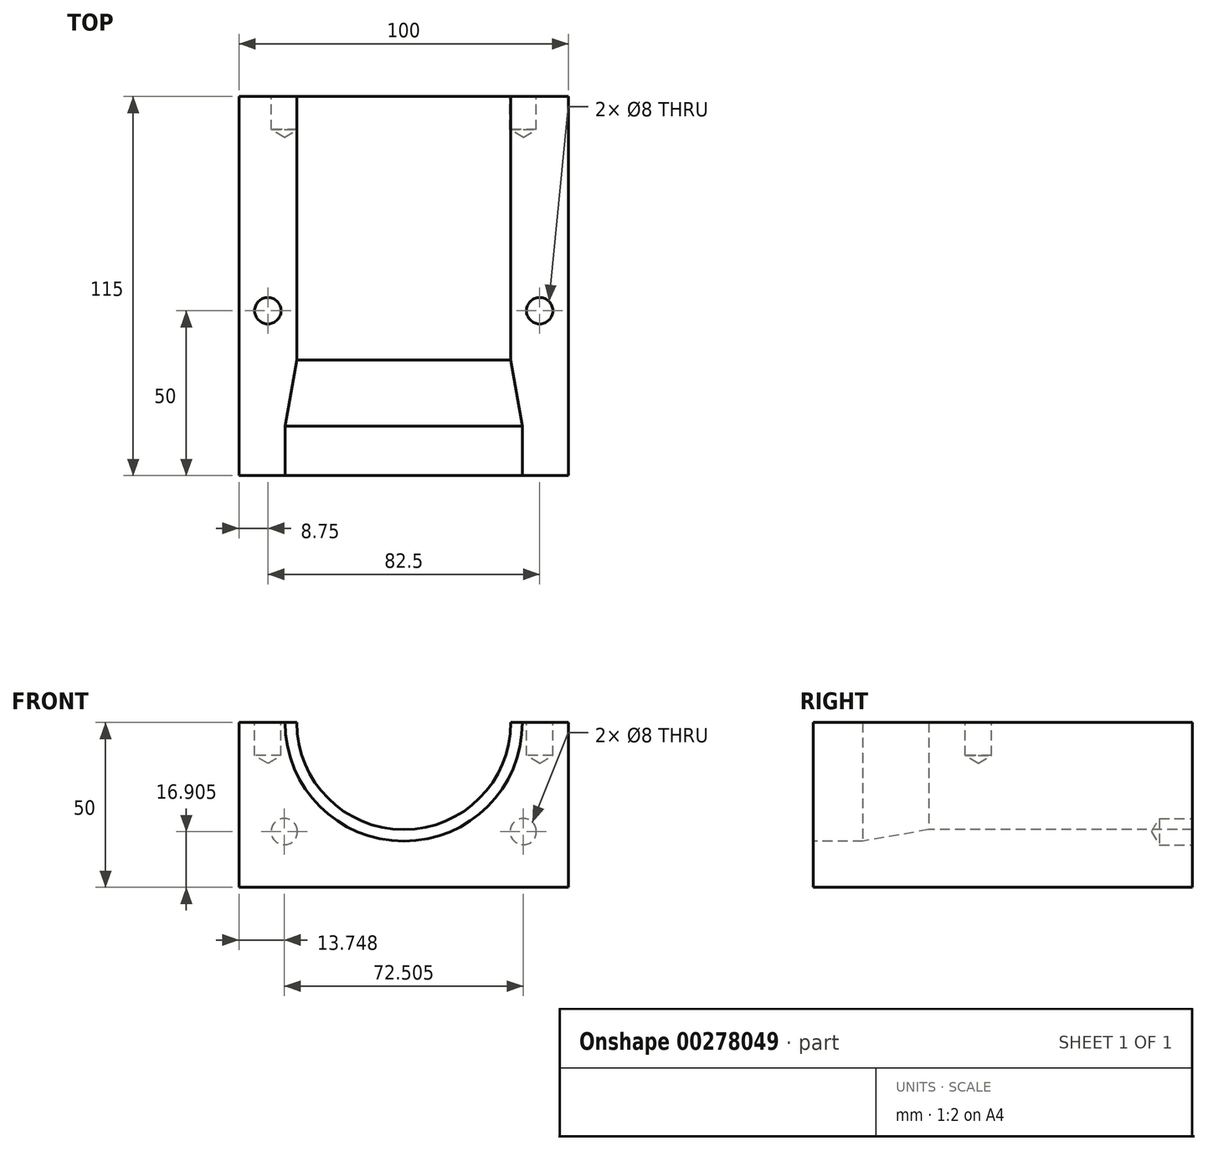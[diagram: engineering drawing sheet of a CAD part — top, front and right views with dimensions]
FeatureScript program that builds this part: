
annotation { "Feature Type Name" : "Feature", "Feature Type Description" : "" }
export const myFeature = defineFeature(function(context is Context, id is Id, definition is map)
    precondition{}
    {
        {
            var Q0;
            Q0=qCreatedBy(makeId("Top.planeOp"),FACE);
            var sketch = newSketch(context, id + "F0", { "sketchPlane" : qUnion([Q0])});
            skLineSegment(sketch, "E0", {"start": v(0, 0) * mm, "end": v(-36, 0) * mm});
            skLineSegment(sketch, "E1", {"start": v(-36, 0) * mm, "end": v(-36, 15) * mm});
            skLineSegment(sketch, "E2", {"start": v(-32.5, 35) * mm, "end": v(-32.5, 125) * mm});
            skLineSegment(sketch, "E3", {"start": v(-32.5, 125) * mm, "end": v(0, 125) * mm});
            skLineSegment(sketch, "E4", {"start": v(0, 125) * mm, "end": v(0, 0) * mm});
            skLineSegment(sketch, "E5", {"start": v(-36, 15) * mm, "end": v(-32.5, 35) * mm});
            skSolve(sketch);
        }
        {
            var Q0;
            Q0=qCreatedBy(makeId("Top.planeOp"),FACE);
            var sketch = newSketch(context, id + "F1", { "sketchPlane" : qUnion([Q0])});
            skLineSegment(sketch, "E6", {"start": v(0, 0) * mm, "end": v(50, 0) * mm});
            skLineSegment(sketch, "E7", {"start": v(50, 0) * mm, "end": v(50, 125) * mm});
            skLineSegment(sketch, "E8", {"start": v(50, 125) * mm, "end": v(-50, 125) * mm});
            skLineSegment(sketch, "E9", {"start": v(-50, 125) * mm, "end": v(-50, 0) * mm});
            skLineSegment(sketch, "E10", {"start": v(-50, 0) * mm, "end": v(0, 0) * mm});
            skSolve(sketch);
        }
        {
            var Q0;
            Q0 = qSketchRegion(id + "F1", true);
            extrude(context, id + "F2", {"entities" : qUnion([Q0]), "oppositeDirection" : true, "depth" : 50 * mm});
        }
        {
            var Q0;
            Q0 = qSketchRegion(id + "F0", true);
            var Q1;
            Q1=sQuery(id+"F0.wireOp",EDGE,"E4");
            revolve(context, id + "F3", {"operationType" : NewBodyOperationType.REMOVE, "entities" : qUnion([Q0]), "axis" : qUnion([Q1]), "revolveType" : RevolveType.FULL, "oppositeDirection" : true});
        }
        {
            var Q0;
            {var subQ0=sQuery(id+"F1.wireOp",EDGE,"E8");var subQ1=sQuery(id+"F1.wireOp",EDGE,"E7");var subQ2=sQuery(id+"F1.wireOp",EDGE,"E10");var subQ3=sQuery(id+"F1.wireOp",EDGE,"E6");Q0=makeQuery(id+"F3.boolean.opBoolean","SPLIT",FACE,{"disambiguationData":[TD([makeQuery(id+"F2.opExtrude","SWEPT_FACE",FACE,{"disambiguationData":[OSD([subQ1])]})])],"derivedFrom":makeQuery(id+"F2.opExtrude","CAP_FACE",FACE,{"disambiguationData":[OSD([subQ3,subQ1,subQ0,sQuery(id+"F1.wireOp",EDGE,"E9"),subQ2])],"isStart":true})});}
            var sketch = newSketch(context, id + "F4", { "sketchPlane" : qUnion([Q0])});
            skLineSegment(sketch, "E11", {"start": v(-41.25, 125) * mm, "end": v(-41.25, 50) * mm});
            skLineSegment(sketch, "E12", {"start": v(-41.25, 50) * mm, "end": v(41.25, 50) * mm});
            skSolve(sketch);
        }
        {
            var Q0;
            Q0=sQuery(id+"F4.wireOp",VERTEX,"E12.start");
            var Q1;
            Q1=sQuery(id+"F4.wireOp",VERTEX,"E12.end");
            var Q2;
            Q2=makeQuery(id+"F2.opExtrude","SWEPT_BODY",BODY,{"disambiguationData":[OSD([sQuery(id+"F1.wireOp",EDGE,"E6"),sQuery(id+"F1.wireOp",EDGE,"E7"),sQuery(id+"F1.wireOp",EDGE,"E8"),sQuery(id+"F1.wireOp",EDGE,"E9"),sQuery(id+"F1.wireOp",EDGE,"E10")])]});
            hole(context, id + "F5", {"style" : HoleStyle.SIMPLE, "endStyle" : HoleEndStyle.BLIND, "holeDiameter" : 8 * mm, "holeDepth" : 10 * mm, "tappedDepth" : 12 * mm, "tapClearance" : 3, "startFromSketch" : true, "locations" : qUnion([Q0, Q1]), "scope" : qUnion([Q2])});
        }
        {
            var Q0;
            Q0=makeQuery(id+"F2.opExtrude","SWEPT_FACE",FACE,{"disambiguationData":[OSD([sQuery(id+"F1.wireOp",EDGE,"E8")])]});
            var sketch = newSketch(context, id + "F6", { "sketchPlane" : qUnion([Q0])});
            skLineSegment(sketch, "E13", {"start": v(0, -50) * mm, "end": v(36.25, -33.1) * mm});
            skPoint(sketch, "E13.endSnap0", {"position": v(0.28, -33.1) * mm});
            skLineSegment(sketch, "E14.MirrorCS", {"start": v(0, -50) * mm, "end": v(-36.25, -33.1) * mm});
            skSolve(sketch);
        }
        {
            var Q0;
            Q0=sQuery(id+"F6.wireOp",VERTEX,"E14.MirrorCS.end");
            var Q1;
            Q1=sQuery(id+"F6.wireOp",VERTEX,"E13.end");
            var Q2;
            Q2=makeQuery(id+"F2.opExtrude","SWEPT_BODY",BODY,{"disambiguationData":[OSD([sQuery(id+"F1.wireOp",EDGE,"E6"),sQuery(id+"F1.wireOp",EDGE,"E7"),sQuery(id+"F1.wireOp",EDGE,"E8"),sQuery(id+"F1.wireOp",EDGE,"E9"),sQuery(id+"F1.wireOp",EDGE,"E10")])]});
            hole(context, id + "F7", {"style" : HoleStyle.SIMPLE, "endStyle" : HoleEndStyle.BLIND, "holeDiameter" : 8 * mm, "holeDepth" : 20 * mm, "tappedDepth" : 12 * mm, "tapClearance" : 3, "startFromSketch" : true, "locations" : qUnion([Q0, Q1]), "scope" : qUnion([Q2])});
        }
        {
            var Q0;
            Q0=makeQuery(id+"F2.opExtrude","SWEPT_FACE",FACE,{"disambiguationData":[OSD([sQuery(id+"F1.wireOp",EDGE,"E8")])]});
            extrude(context, id + "F8", {"entities" : qUnion([Q0]), "operationType" : NewBodyOperationType.REMOVE, "oppositeDirection" : true, "depth" : 10 * mm});
        }
    });
